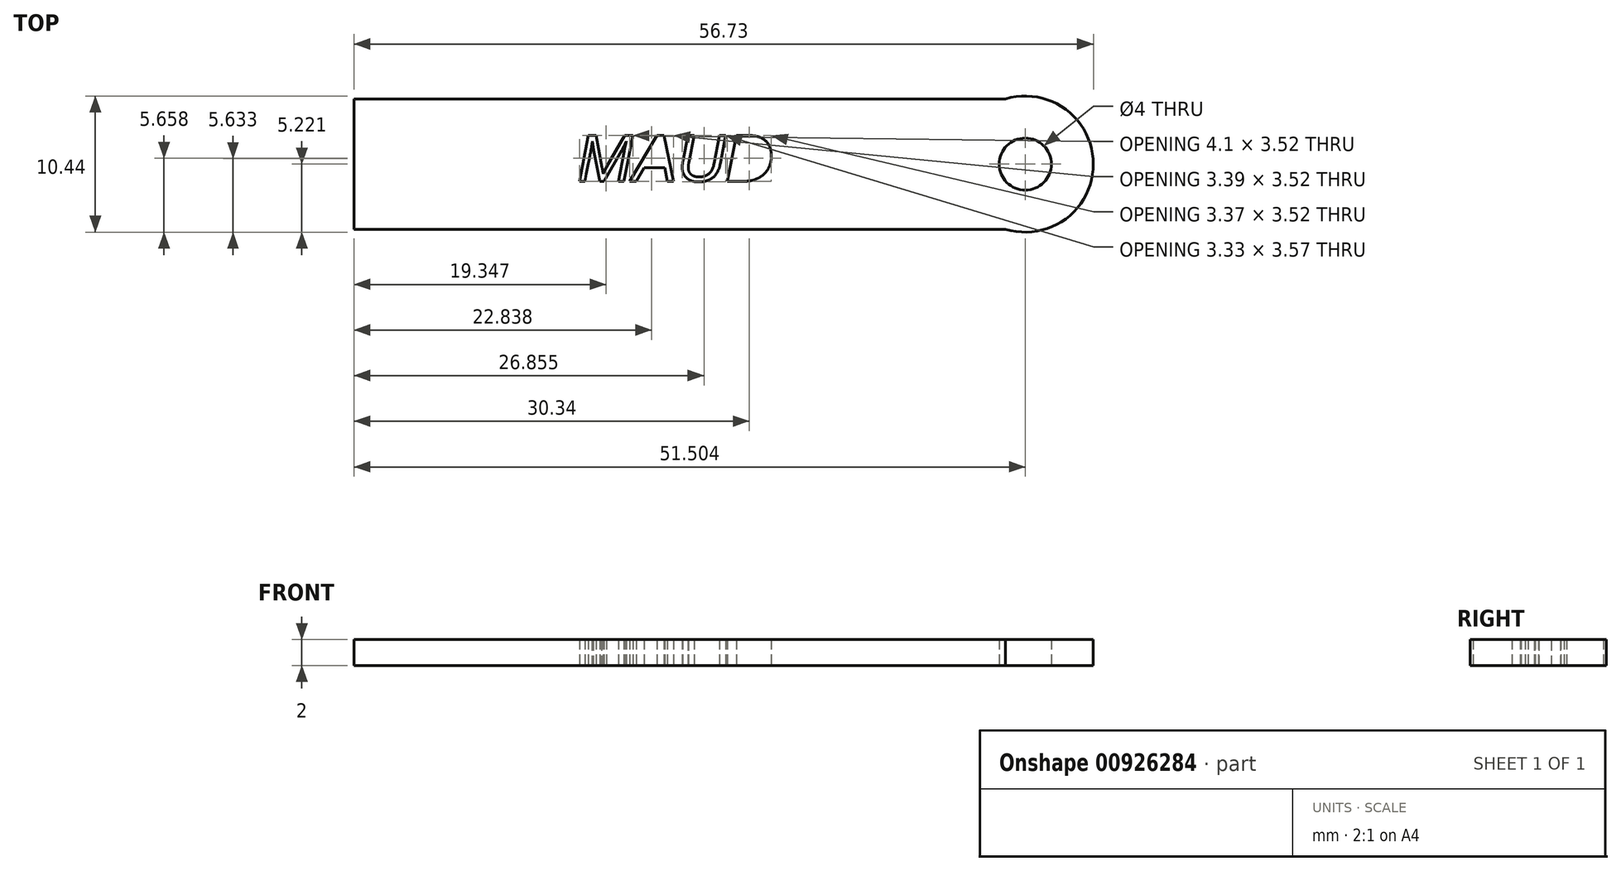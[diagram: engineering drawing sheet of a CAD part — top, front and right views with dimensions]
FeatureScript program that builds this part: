
annotation { "Feature Type Name" : "Feature", "Feature Type Description" : "" }
export const myFeature = defineFeature(function(context is Context, id is Id, definition is map)
    precondition{}
    {
        {
            var Q0;
            Q0=qCreatedBy(makeId("Top.planeOp"),FACE);
            var sketch = newSketch(context, id + "F0", { "sketchPlane" : qUnion([Q0])});
            skLineSegment(sketch, "E0.bottom", {"start": v(-34.31, 26.11) * mm, "end": v(15.69, 26.11) * mm});
            skLineSegment(sketch, "E0.top", {"start": v(-34.31, 16.11) * mm, "end": v(15.69, 16.11) * mm});
            skLineSegment(sketch, "E0.left", {"start": v(-34.31, 26.11) * mm, "end": v(-34.31, 16.11) * mm});
            skArc(sketch, "E1", {"start": v(15.69, 16.11) * mm, "mid": v(22.42, 21.11) * mm, "end": v(15.69, 26.11) * mm});
            skCircle(sketch, "E2", {"center": v(17.2, 21.11) * mm, "radius": 2 * mm});
            skText(sketch, "E3", { "text": "MAUD", "fontName": "Arimo-Italic.ttf"});
            const initialGuessF0  = {"E3": [-0.01717, 0.01979, 1, 0, 0.00368]};
            skSetInitialGuess(sketch, initialGuessF0);
            skSolve(sketch);
        }
        {
            var Q0;
            Q0 = qSketchRegion(id + "F0", true);
            extrude(context, id + "F1", {"entities" : qUnion([Q0]), "depth" : 2 * mm, "offsetDistance" : 25 * mm});
        }
    });
